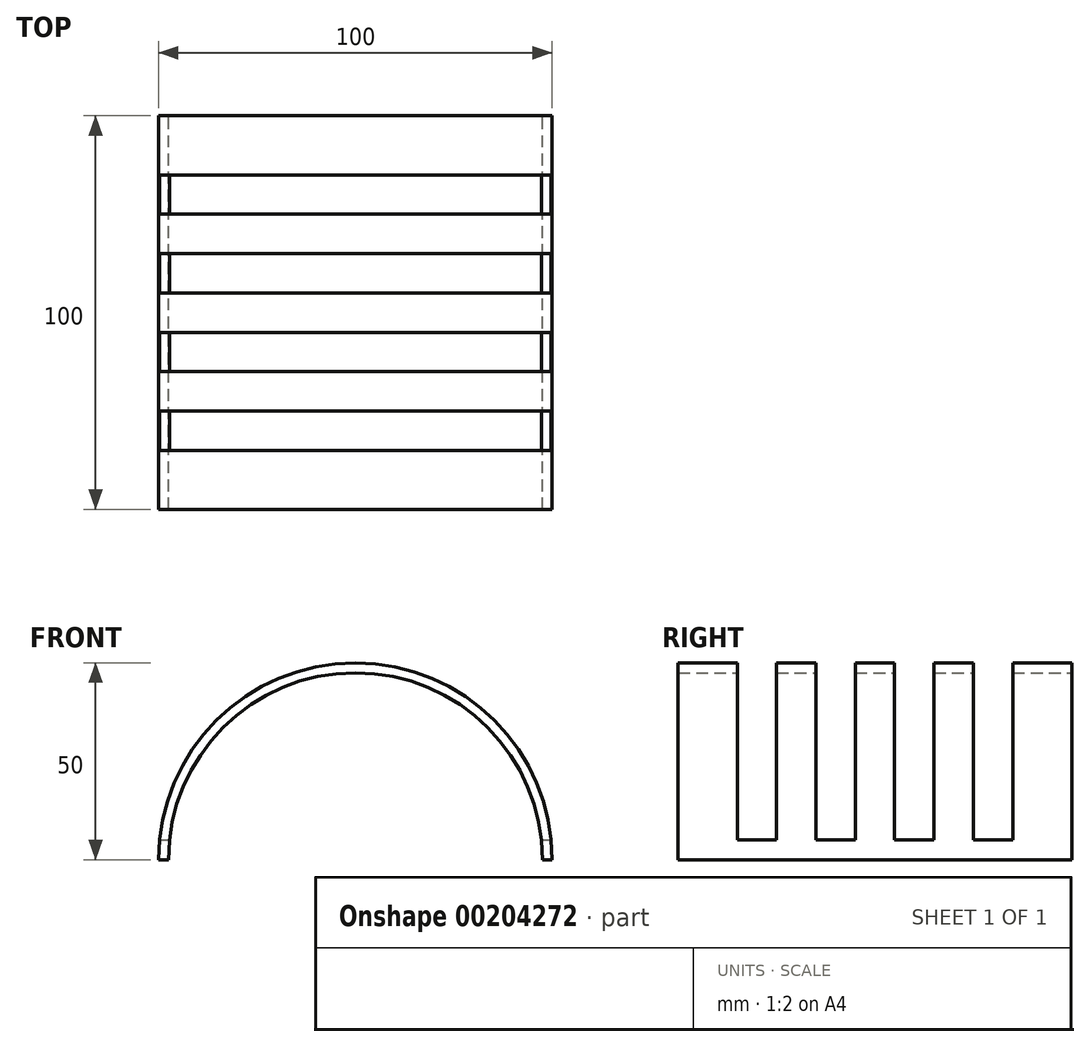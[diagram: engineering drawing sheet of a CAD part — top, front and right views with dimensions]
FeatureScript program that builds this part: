
annotation { "Feature Type Name" : "Feature", "Feature Type Description" : "" }
export const myFeature = defineFeature(function(context is Context, id is Id, definition is map)
    precondition{}
    {
        {
            var Q0;
            Q0=qCreatedBy(makeId("Front.planeOp"),FACE);
            var sketch = newSketch(context, id + "F0", { "sketchPlane" : qUnion([Q0])});
            skArc(sketch, "E0", {"start": v(47.5, 0) * mm, "mid": v(0, 47.5) * mm, "end": v(-47.5, 0) * mm});
            skArc(sketch, "E1", {"start": v(50, 0) * mm, "mid": v(0, 50) * mm, "end": v(-50, 0) * mm});
            skLineSegment(sketch, "E2", {"start": v(-50, 0) * mm, "end": v(-47.5, 0) * mm});
            skLineSegment(sketch, "E3.trimOffspring", {"start": v(47.5, 0) * mm, "end": v(50, 0) * mm});
            skSolve(sketch);
        }
        {
            var Q0;
            Q0 = qSketchRegion(id + "F0", true);
            extrude(context, id + "F1", {"entities" : qUnion([Q0]), "endBound" : BoundingType.SYMMETRIC, "depth" : 100 * mm});
        }
        {
            var Q0;
            Q0=qCreatedBy(makeId("Right.planeOp"),FACE);
            var sketch = newSketch(context, id + "F2", { "sketchPlane" : qUnion([Q0])});
            skLineSegment(sketch, "E4.bottom", {"start": v(-35, 5) * mm, "end": v(0, 5) * mm});
            skLineSegment(sketch, "E4.top", {"start": v(-35, 62.96) * mm, "end": v(0, 62.96) * mm});
            skLineSegment(sketch, "E4.left", {"start": v(-35, 5) * mm, "end": v(-35, 62.96) * mm});
            skLineSegment(sketch, "E5", {"start": v(-25, 62.96) * mm, "end": v(-25, 5) * mm});
            skLineSegment(sketch, "E6", {"start": v(-5, 62.96) * mm, "end": v(-5, 5) * mm});
            skLineSegment(sketch, "E7", {"start": v(-15, 62.96) * mm, "end": v(-15, 5) * mm});
            skLineSegment(sketch, "E8.MirrorCS", {"start": v(35, 5) * mm, "end": v(35, 62.96) * mm});
            skLineSegment(sketch, "E9.MirrorCS", {"start": v(15, 62.96) * mm, "end": v(15, 5) * mm});
            skLineSegment(sketch, "E10.MirrorCS", {"start": v(5, 62.96) * mm, "end": v(5, 5) * mm});
            skLineSegment(sketch, "E11.MirrorCS", {"start": v(35, 5) * mm, "end": v(0, 5) * mm});
            skLineSegment(sketch, "E12.MirrorCS", {"start": v(25, 62.96) * mm, "end": v(25, 5) * mm});
            skLineSegment(sketch, "E13.MirrorCS", {"start": v(35, 62.96) * mm, "end": v(0, 62.96) * mm});
            skSolve(sketch);
        }
        {
            var Q0;
            {var subQ0=sQuery(id+"F2.wireOp",EDGE,"E4.left");Q0=makeQuery(id+"F2.imprint","IMPRINT",FACE,{"disambiguationData":[TD([[makeQuery(id+"F2.imprint","IMPRINT",EDGE,{"derivedFrom":subQ0}),-1.0]])]});}
            var Q1;
            {var subQ0=sQuery(id+"F2.wireOp",EDGE,"E8.MirrorCS");Q1=makeQuery(id+"F2.imprint","IMPRINT",FACE,{"disambiguationData":[TD([[makeQuery(id+"F2.imprint","IMPRINT",EDGE,{"derivedFrom":subQ0}),1.0]])]});}
            var Q2;
            {var subQ0=sQuery(id+"F2.wireOp",EDGE,"E6");Q2=makeQuery(id+"F2.imprint","IMPRINT",FACE,{"disambiguationData":[TD([[makeQuery(id+"F2.imprint","IMPRINT",EDGE,{"derivedFrom":subQ0}),-1.0]])]});}
            var Q3;
            {var subQ0=sQuery(id+"F2.wireOp",EDGE,"E9.MirrorCS");Q3=makeQuery(id+"F2.imprint","IMPRINT",FACE,{"disambiguationData":[TD([[makeQuery(id+"F2.imprint","IMPRINT",EDGE,{"derivedFrom":subQ0}),-1.0]])]});}
            extrude(context, id + "F3", {"entities" : qUnion([Q0, Q1, Q2, Q3]), "operationType" : NewBodyOperationType.REMOVE, "endBound" : BoundingType.SYMMETRIC, "oppositeDirection" : true, "depth" : 110 * mm});
        }
    });
